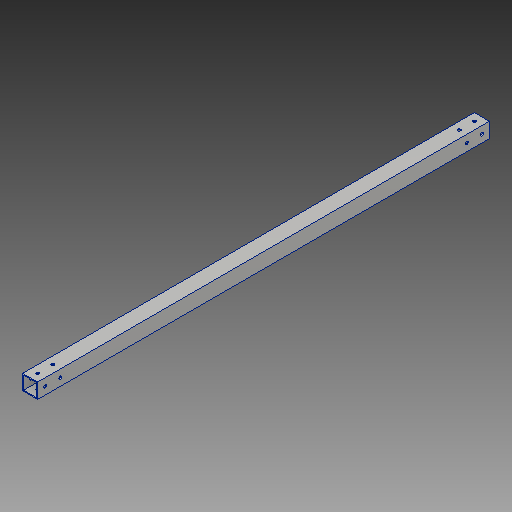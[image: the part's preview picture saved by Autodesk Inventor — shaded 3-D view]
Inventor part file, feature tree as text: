
AUTODESK INVENTOR PART (.ipt)
format: ipt  version: 2018 (Build 220112000, 112)  size: 141,312 bytes
history: native  units: in
note: dims shown in document units (in); Inventor stores cm internally (conversion verified against a paired STEP export)
features: extrude x3, sketch x3
ambient origin geometry x8: Origin, YZ Plane, XZ Plane, XY Plane, X Axis, Y Axis, Z Axis, Center Point
bodies: Solid1 (feature_tree)
feature tree (6):
  extrude  "Extrusion1"  Depth=1.0in
  extrude  "Extrusion2"  Depth=0.0625in
  extrude  "Extrusion3"  Depth=0.0625in
  sketch  "Sketch1"  dims[d0=1.0in d1=1.0in]
  sketch  "Sketch2"  dims[d2=0.0625in d3=0.0625in]
  sketch  "Sketch3"  dims[d4=0.0625in d5=0.0625in d6=30.0in d7=0.0in d8=0.5in d9=1.0in d10=0.5in d11=1.0in d12=0.2in d13=1.0in d14=0.0in d15=0.5in d16=1.0in d17=0.5in d18=1.0in d19=0.2in d20=1.0in d21=0.0in]
